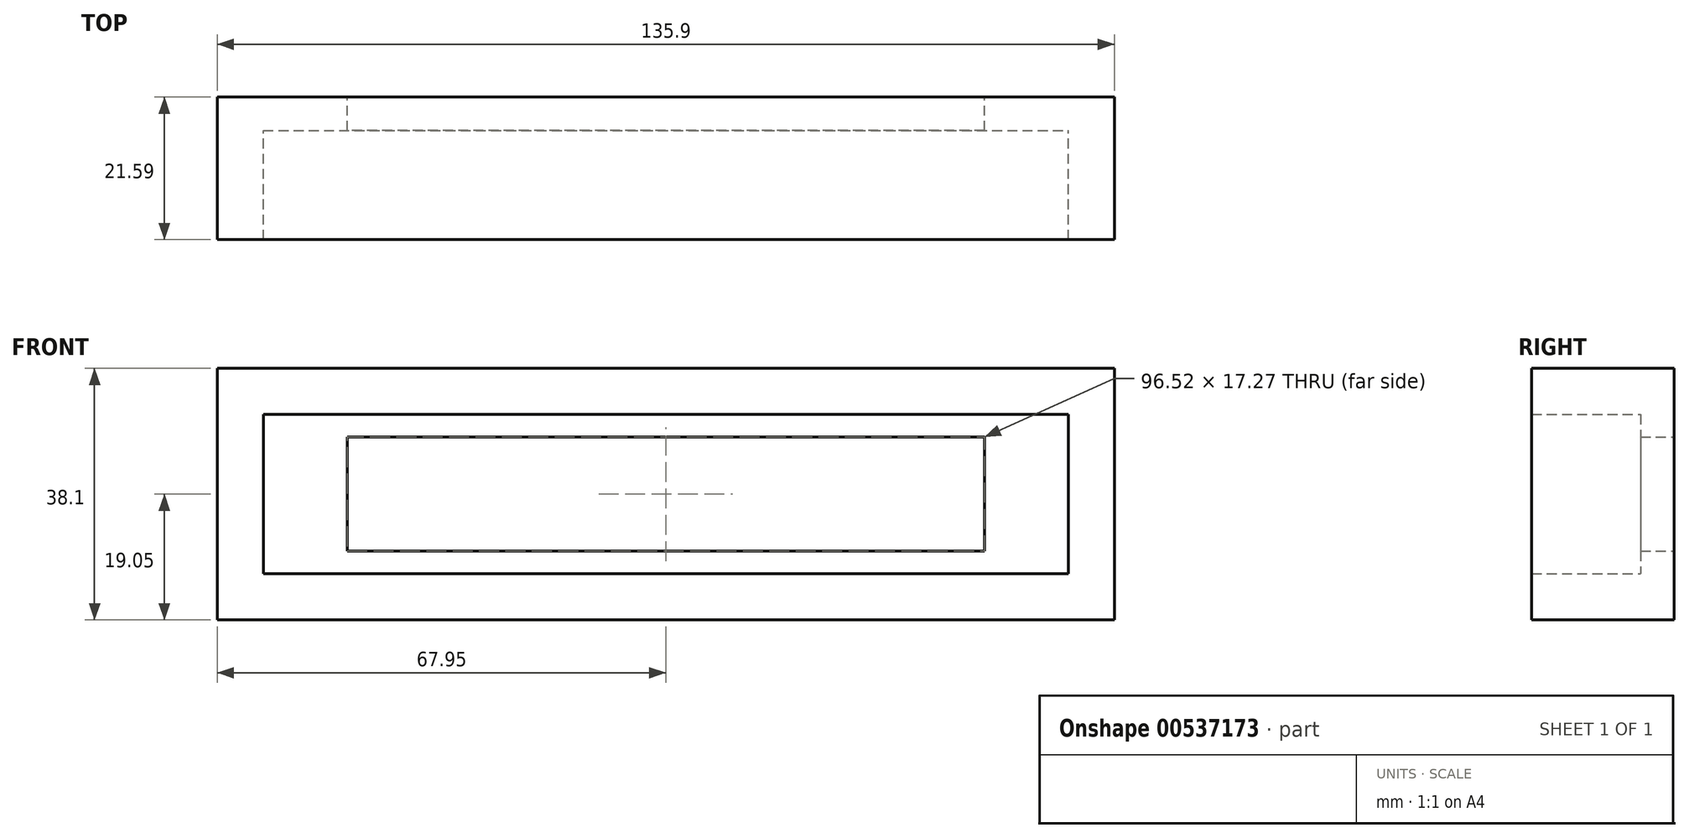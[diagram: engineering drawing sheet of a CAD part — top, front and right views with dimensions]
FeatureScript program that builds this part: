
annotation { "Feature Type Name" : "Feature", "Feature Type Description" : "" }
export const myFeature = defineFeature(function(context is Context, id is Id, definition is map)
    precondition{}
    {
        {
            var Q0;
            Q0=qCreatedBy(makeId("Front.planeOp"),FACE);
            var sketch = newSketch(context, id + "F0", { "sketchPlane" : qUnion([Q0])});
            skLineSegment(sketch, "E0.bottom", {"start": v(48.26, 8.64) * mm, "end": v(-48.26, 8.64) * mm});
            skLineSegment(sketch, "E0.top", {"start": v(48.26, -8.64) * mm, "end": v(-48.26, -8.64) * mm});
            skLineSegment(sketch, "E0.left", {"start": v(48.26, 8.64) * mm, "end": v(48.26, -8.64) * mm});
            skLineSegment(sketch, "E0.right", {"start": v(-48.26, 8.64) * mm, "end": v(-48.26, -8.64) * mm});
            skPoint(sketch, "E0.middle", {"position": v(0, 0) * mm});
            skLineSegment(sketch, "E1.bottom", {"start": v(-60.96, 12.07) * mm, "end": v(60.96, 12.07) * mm});
            skLineSegment(sketch, "E1.top", {"start": v(-60.96, -12.07) * mm, "end": v(60.96, -12.07) * mm});
            skLineSegment(sketch, "E1.left", {"start": v(-60.96, 12.07) * mm, "end": v(-60.96, -12.07) * mm});
            skLineSegment(sketch, "E1.right", {"start": v(60.96, 12.07) * mm, "end": v(60.96, -12.07) * mm});
            skLineSegment(sketch, "E2.bottom", {"start": v(67.95, 19.05) * mm, "end": v(-67.95, 19.05) * mm});
            skLineSegment(sketch, "E2.top", {"start": v(67.95, -19.05) * mm, "end": v(-67.95, -19.05) * mm});
            skLineSegment(sketch, "E2.left", {"start": v(67.95, 19.05) * mm, "end": v(67.95, -19.05) * mm});
            skLineSegment(sketch, "E2.right", {"start": v(-67.95, 19.05) * mm, "end": v(-67.95, -19.05) * mm});
            skSolve(sketch);
        }
        {
            var Q0;
            Q0=makeQuery(id+"F0.imprint","IMPRINT",FACE,{"disambiguationData":[TD([[makeQuery(id+"F0.imprint","IMPRINT",EDGE,{"derivedFrom":sQuery(id+"F0.wireOp",EDGE,"E0.bottom")}),-1.0]])]});
            extrude(context, id + "F1", {"entities" : qUnion([Q0]), "depth" : 5.08 * mm, "offsetDistance" : 25.4 * mm});
        }
        {
            var Q0;
            Q0=qCreatedBy(makeId("Front.planeOp"),FACE);
            var sketch = newSketch(context, id + "F2", { "sketchPlane" : qUnion([Q0])});
            skLineSegment(sketch, "E3.bottom", {"start": v(-67.95, 19.05) * mm, "end": v(67.95, 19.05) * mm});
            skLineSegment(sketch, "E3.top", {"start": v(-67.95, -19.05) * mm, "end": v(67.95, -19.05) * mm});
            skLineSegment(sketch, "E3.left", {"start": v(-67.95, 19.05) * mm, "end": v(-67.95, -19.05) * mm});
            skLineSegment(sketch, "E3.right", {"start": v(67.95, 19.05) * mm, "end": v(67.95, -19.05) * mm});
            skPoint(sketch, "E3.middle", {"position": v(0, 0) * mm});
            skLineSegment(sketch, "E4.bottom", {"start": v(-60.96, 12.06) * mm, "end": v(60.96, 12.06) * mm});
            skLineSegment(sketch, "E4.top", {"start": v(-60.96, -12.06) * mm, "end": v(60.96, -12.06) * mm});
            skLineSegment(sketch, "E4.left", {"start": v(-60.96, 12.06) * mm, "end": v(-60.96, -12.06) * mm});
            skLineSegment(sketch, "E4.right", {"start": v(60.96, 12.06) * mm, "end": v(60.96, -12.06) * mm});
            skSolve(sketch);
        }
        {
            var Q0;
            Q0=makeQuery(id+"F2.imprint","IMPRINT",FACE,{"disambiguationData":[TD([[makeQuery(id+"F2.imprint","IMPRINT",EDGE,{"derivedFrom":sQuery(id+"F2.wireOp",EDGE,"E3.bottom")}),-1.0]])]});
            extrude(context, id + "F3", {"entities" : qUnion([Q0]), "operationType" : NewBodyOperationType.ADD, "depth" : 21.59 * mm, "offsetDistance" : 25.4 * mm});
        }
    });
